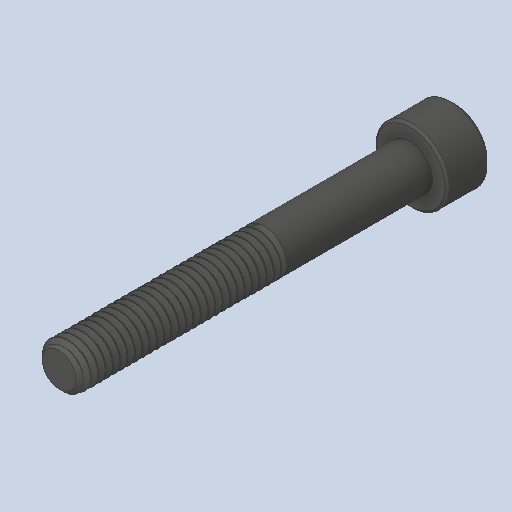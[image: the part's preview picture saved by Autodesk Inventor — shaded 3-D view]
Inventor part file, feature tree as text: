
AUTODESK INVENTOR PART (.ipt)
format: ipt  version: 2023.4 (Build 274418000, 418)  size: 689,152 bytes
history: native  units: in
note: dims shown in document units (in); Inventor stores cm internally (conversion verified against a paired STEP export)
features: chamfer x1
ambient origin geometry x8: Origin, YZ Plane, XZ Plane, XY Plane, X Axis, Y Axis, Z Axis, Center Point
bodies: Solid1 (feature_tree)
feature tree (1):
  chamfer  "Chamfer2"  [1 undecoded]
note: 1 required parameter value undecoded (feature->parameter linkage not recoverable at this tier; creation-order binding heuristic only, values carry confidence <= 0.55)
